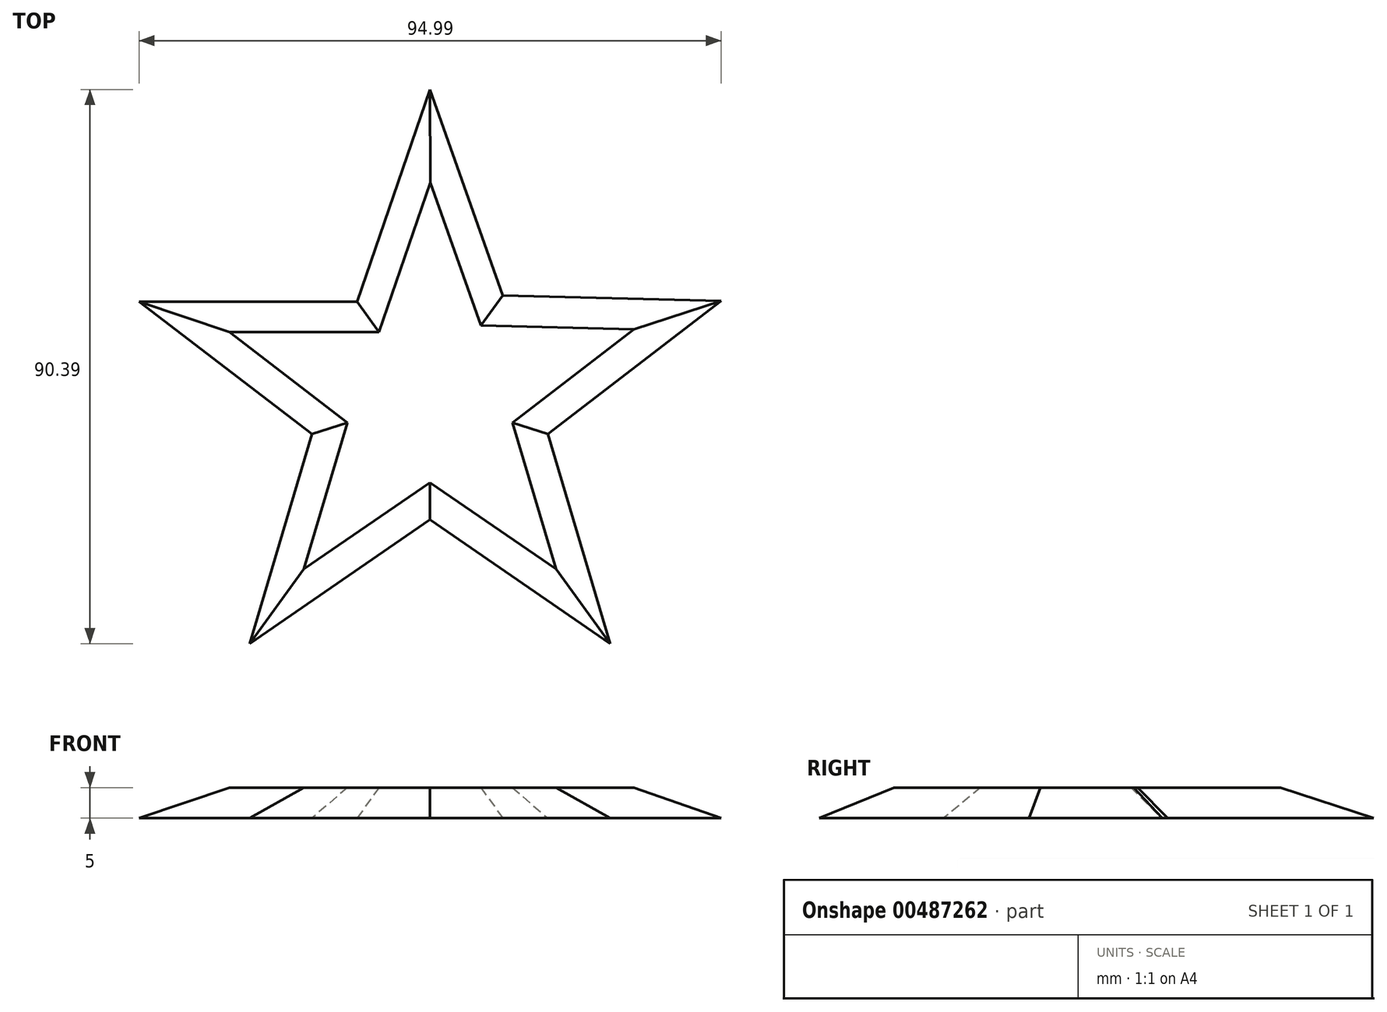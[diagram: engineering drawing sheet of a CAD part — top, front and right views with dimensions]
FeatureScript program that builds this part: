
annotation { "Feature Type Name" : "Feature", "Feature Type Description" : "" }
export const myFeature = defineFeature(function(context is Context, id is Id, definition is map)
    precondition{}
    {
        {
            var Q0;
            Q0=qCreatedBy(makeId("Top.planeOp"),FACE);
            var sketch = newSketch(context, id + "F0", { "sketchPlane" : qUnion([Q0])});
            skPoint(sketch, "E0.0.midPoint", {"position": v(0, -42.87) * mm});
            skLineSegment(sketch, "E1", {"start": v(0, 52.99) * mm, "end": v(-12.6, 16.37) * mm});
            skPoint(sketch, "E1.endSnap0", {"position": v(-12.6, 17.34) * mm});
            skLineSegment(sketch, "E2", {"start": v(-12.6, 16.37) * mm, "end": v(-50.4, 16.37) * mm});
            skLineSegment(sketch, "E3", {"start": v(-20.38, -6.62) * mm, "end": v(-50.4, 16.37) * mm});
            skLineSegment(sketch, "E4", {"start": v(-20.38, -6.62) * mm, "end": v(-31.15, -42.87) * mm});
            skLineSegment(sketch, "E5", {"start": v(0, -21.43) * mm, "end": v(-31.15, -42.87) * mm});
            skLineSegment(sketch, "E6", {"start": v(0, -21.43) * mm, "end": v(31.15, -42.87) * mm});
            skLineSegment(sketch, "E7", {"start": v(20.38, -6.62) * mm, "end": v(31.15, -42.87) * mm});
            skLineSegment(sketch, "E8", {"start": v(20.38, -6.62) * mm, "end": v(50.4, 16.37) * mm});
            skLineSegment(sketch, "E9", {"start": v(12.6, 17.34) * mm, "end": v(50.4, 16.37) * mm});
            skLineSegment(sketch, "E10", {"start": v(12.6, 17.34) * mm, "end": v(0, 52.99) * mm});
            skLineSegment(sketch, "E11", {"start": v(0, 52.99) * mm, "end": v(0, 0) * mm});
            skLineSegment(sketch, "E12", {"start": v(0, 0) * mm, "end": v(50.4, 16.37) * mm});
            skLineSegment(sketch, "E13", {"start": v(31.15, -42.87) * mm, "end": v(0, 0) * mm});
            skLineSegment(sketch, "E14", {"start": v(0, 0) * mm, "end": v(-31.15, -42.87) * mm});
            skLineSegment(sketch, "E15", {"start": v(-50.4, 16.37) * mm, "end": v(0, 0) * mm});
            skLineSegment(sketch, "E16", {"start": v(12.6, 17.34) * mm, "end": v(0, 0) * mm});
            skLineSegment(sketch, "E17", {"start": v(20.38, -6.62) * mm, "end": v(0, 0) * mm});
            skLineSegment(sketch, "E18", {"start": v(0, -21.43) * mm, "end": v(0, 0) * mm});
            skLineSegment(sketch, "E19", {"start": v(-20.38, -6.62) * mm, "end": v(0, 0) * mm});
            skLineSegment(sketch, "E20", {"start": v(-12.6, 16.37) * mm, "end": v(0, 0) * mm});
            skSolve(sketch);
        }
        {
            var Q0;
            Q0 = qSketchRegion(id + "F0", true);
            extrude(context, id + "F1", {"entities" : qUnion([Q0]), "depth" : 5 * mm, "offsetDistance" : 25 * mm});
        }
        {
            var Q0;
            Q0=makeQuery(id+"F1.opExtrude","CAP_FACE",FACE,{"disambiguationData":[OSD([sQuery(id+"F0.wireOp",EDGE,"E1"),sQuery(id+"F0.wireOp",EDGE,"E2"),sQuery(id+"F0.wireOp",EDGE,"E3"),sQuery(id+"F0.wireOp",EDGE,"E4"),sQuery(id+"F0.wireOp",EDGE,"E5"),sQuery(id+"F0.wireOp",EDGE,"E6"),sQuery(id+"F0.wireOp",EDGE,"E7"),sQuery(id+"F0.wireOp",EDGE,"E8"),sQuery(id+"F0.wireOp",EDGE,"E9"),sQuery(id+"F0.wireOp",EDGE,"E10")])],"isStart":false});
            chamfer(context, id + "F2", {"entities" : qUnion([Q0]), "width" : 6 * mm, "tangentPropagation" : true});
        }
    });
